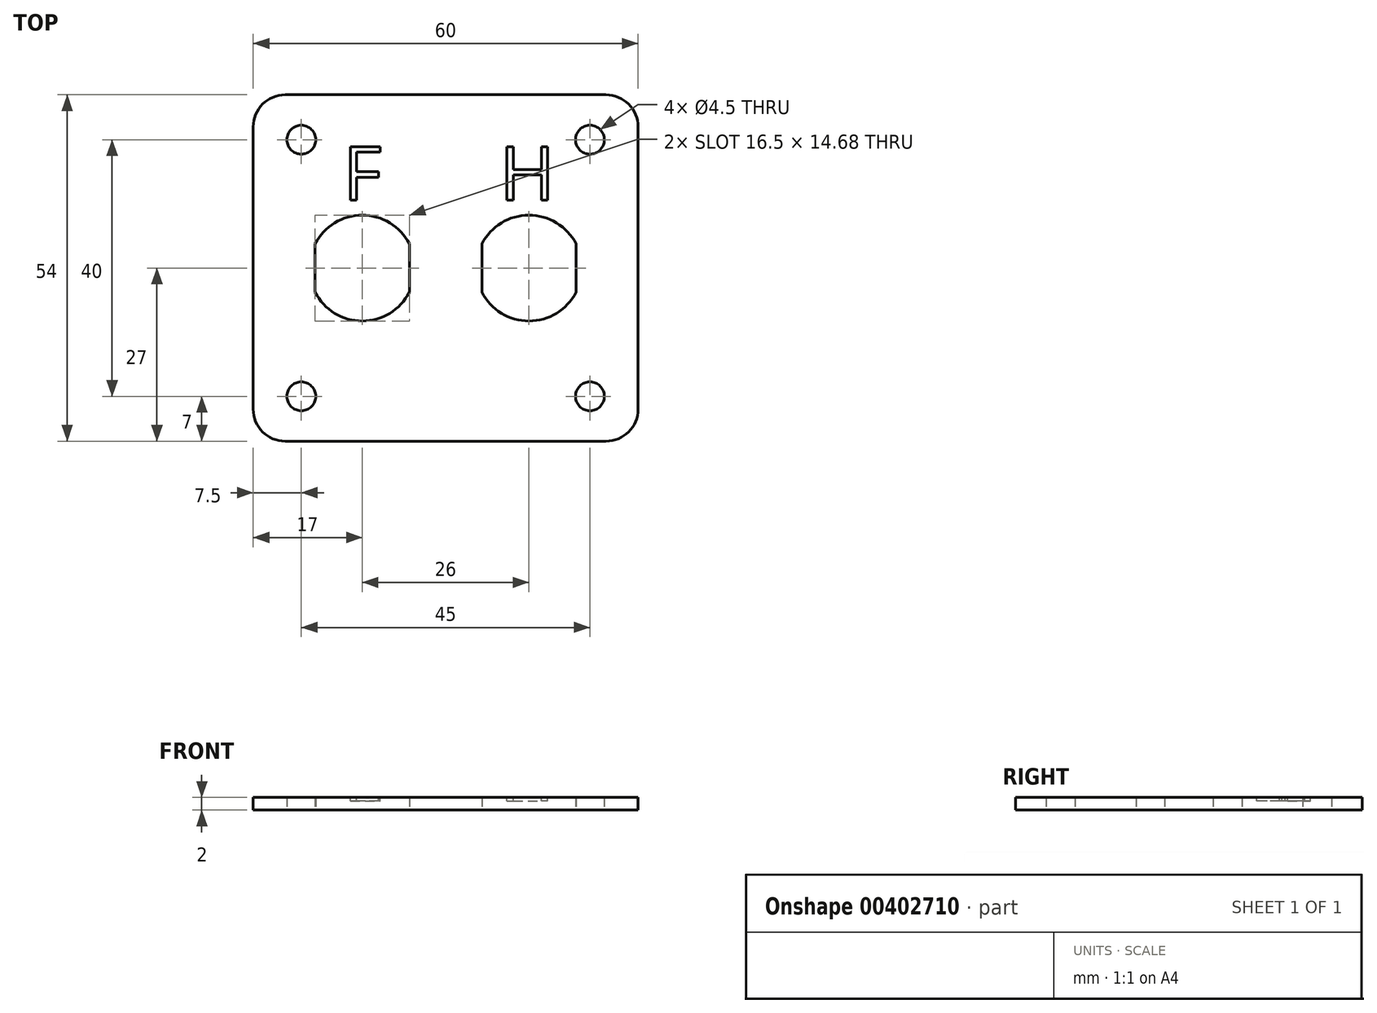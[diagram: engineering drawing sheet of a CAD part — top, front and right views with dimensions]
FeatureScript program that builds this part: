
annotation { "Feature Type Name" : "Feature", "Feature Type Description" : "" }
export const myFeature = defineFeature(function(context is Context, id is Id, definition is map)
    precondition{}
    {
        {
            var Q0;
            Q0=qCreatedBy(makeId("Top.planeOp"),FACE);
            var sketch = newSketch(context, id + "F0", { "sketchPlane" : qUnion([Q0])});
            skLineSegment(sketch, "E0.bottom", {"start": v(30, -27) * mm, "end": v(-30, -27) * mm});
            skLineSegment(sketch, "E0.top", {"start": v(30, 27) * mm, "end": v(-30, 27) * mm});
            skLineSegment(sketch, "E0.left", {"start": v(30, -27) * mm, "end": v(30, 27) * mm});
            skLineSegment(sketch, "E0.right", {"start": v(-30, -27) * mm, "end": v(-30, 27) * mm});
            skPoint(sketch, "E0.middle", {"position": v(0, 0) * mm});
            skLineSegment(sketch, "E1.bottom", {"start": v(22.5, -20) * mm, "end": v(-22.5, -20) * mm});
            skLineSegment(sketch, "E1.top", {"start": v(22.5, 20) * mm, "end": v(-22.5, 20) * mm});
            skLineSegment(sketch, "E1.left", {"start": v(22.5, -20) * mm, "end": v(22.5, 20) * mm});
            skLineSegment(sketch, "E1.right", {"start": v(-22.5, -20) * mm, "end": v(-22.5, 20) * mm});
            skPoint(sketch, "E2", {"position": v(13, 0) * mm});
            skPoint(sketch, "E3", {"position": v(-13, 0) * mm});
            skPoint(sketch, "E4", {"position": v(2.46, -38.07) * mm});
            skCircle(sketch, "E5", {"center": v(13, 0) * mm, "radius": 8.25 * mm});
            skCircle(sketch, "E6", {"center": v(-13, 0) * mm, "radius": 8.25 * mm});
            skPoint(sketch, "E7", {"position": v(-22.5, 20) * mm});
            skPoint(sketch, "E8", {"position": v(-22.5, -20) * mm});
            skPoint(sketch, "E9", {"position": v(22.5, -20) * mm});
            skPoint(sketch, "E10", {"position": v(22.5, 20) * mm});
            skLineSegment(sketch, "E11.bottom", {"start": v(-5.66, -3.77) * mm, "end": v(-20.34, -3.77) * mm});
            skLineSegment(sketch, "E11.top", {"start": v(-5.66, 3.77) * mm, "end": v(-20.34, 3.77) * mm});
            skLineSegment(sketch, "E11.left", {"start": v(-5.66, -3.77) * mm, "end": v(-5.66, 3.77) * mm});
            skLineSegment(sketch, "E11.right", {"start": v(-20.34, -3.77) * mm, "end": v(-20.34, 3.77) * mm});
            skLineSegment(sketch, "E12.bottom", {"start": v(5.66, -3.77) * mm, "end": v(20.34, -3.77) * mm});
            skLineSegment(sketch, "E12.top", {"start": v(5.66, 3.77) * mm, "end": v(20.34, 3.77) * mm});
            skLineSegment(sketch, "E12.left", {"start": v(5.66, -3.77) * mm, "end": v(5.66, 3.77) * mm});
            skLineSegment(sketch, "E12.right", {"start": v(20.34, -3.77) * mm, "end": v(20.34, 3.77) * mm});
            skSolve(sketch);
        }
        {
            var Q0;
            {var subQ0=sQuery(id+"F0.wireOp",EDGE,"8MdXUvT1-A3xL-WGTa-ljN5-XWlnOgiy7zjZ.right");Q0=makeQuery(id+"F0.imprint","IMPRINT",FACE,{"disambiguationData":[TD([[makeQuery(id+"F0.imprint","IMPRINT",EDGE,{"derivedFrom":subQ0}),1.0]])]});}
            var Q1;
            {var subQ0=sQuery(id+"F0.wireOp",EDGE,"wU3xxOYv-X3oH-PTcr-ihHl-F4pvzyvM6u1C.left");Q1=makeQuery(id+"F0.imprint","IMPRINT",FACE,{"disambiguationData":[TD([[makeQuery(id+"F0.imprint","IMPRINT",EDGE,{"derivedFrom":subQ0}),1.0]])]});}
            var Q2;
            {var subQ0=sQuery(id+"F0.wireOp",EDGE,"wU3xxOYv-X3oH-PTcr-ihHl-F4pvzyvM6u1C.right");Q2=makeQuery(id+"F0.imprint","IMPRINT",FACE,{"disambiguationData":[TD([[makeQuery(id+"F0.imprint","IMPRINT",EDGE,{"derivedFrom":subQ0}),-1.0]])]});}
            var Q3;
            {var subQ0=sQuery(id+"F0.wireOp",EDGE,"8MdXUvT1-A3xL-WGTa-ljN5-XWlnOgiy7zjZ.left");Q3=makeQuery(id+"F0.imprint","IMPRINT",FACE,{"disambiguationData":[TD([[makeQuery(id+"F0.imprint","IMPRINT",EDGE,{"derivedFrom":subQ0}),-1.0]])]});}
            var Q4;
            Q4=makeQuery(id+"F0.imprint","IMPRINT",FACE,{"disambiguationData":[TD([[makeQuery(id+"F0.imprint","IMPRINT",EDGE,{"derivedFrom":sQuery(id+"F0.wireOp",EDGE,"E1.bottom")}),-1.0]])]});
            var Q5;
            Q5=makeQuery(id+"F0.imprint","IMPRINT",FACE,{"disambiguationData":[TD([[makeQuery(id+"F0.imprint","IMPRINT",EDGE,{"derivedFrom":sQuery(id+"F0.wireOp",EDGE,"E0.bottom")}),-1.0]])]});
            var Q6;
            {var subQ0=sQuery(id+"F0.wireOp",EDGE,"E11.right");Q6=makeQuery(id+"F0.imprint","IMPRINT",FACE,{"disambiguationData":[TD([[makeQuery(id+"F0.imprint","IMPRINT",EDGE,{"derivedFrom":subQ0}),1.0]])]});}
            var Q7;
            {var subQ0=sQuery(id+"F0.wireOp",EDGE,"E11.left");Q7=makeQuery(id+"F0.imprint","IMPRINT",FACE,{"disambiguationData":[TD([[makeQuery(id+"F0.imprint","IMPRINT",EDGE,{"derivedFrom":subQ0}),-1.0]])]});}
            var Q8;
            {var subQ0=sQuery(id+"F0.wireOp",EDGE,"E12.left");Q8=makeQuery(id+"F0.imprint","IMPRINT",FACE,{"disambiguationData":[TD([[makeQuery(id+"F0.imprint","IMPRINT",EDGE,{"derivedFrom":subQ0}),1.0]])]});}
            var Q9;
            {var subQ0=sQuery(id+"F0.wireOp",EDGE,"E12.right");Q9=makeQuery(id+"F0.imprint","IMPRINT",FACE,{"disambiguationData":[TD([[makeQuery(id+"F0.imprint","IMPRINT",EDGE,{"derivedFrom":subQ0}),-1.0]])]});}
            extrude(context, id + "F1", {"entities" : qUnion([Q0, Q1, Q2, Q3, Q4, Q5, Q6, Q7, Q8, Q9]), "depth" : 2 * mm});
        }
        {
            var Q0;
            Q0=sQuery(id+"F0.wireOp",VERTEX,"E7");
            var Q1;
            Q1=sQuery(id+"F0.wireOp",VERTEX,"E8");
            var Q2;
            Q2=sQuery(id+"F0.wireOp",VERTEX,"E9");
            var Q3;
            Q3=sQuery(id+"F0.wireOp",VERTEX,"E10");
            var Q4;
            Q4=makeQuery(id+"F1.opExtrude","SWEPT_BODY",BODY,{"disambiguationData":[OSD([sQuery(id+"F0.wireOp",EDGE,"E0.bottom"),sQuery(id+"F0.wireOp",EDGE,"E0.top"),sQuery(id+"F0.wireOp",EDGE,"E0.left"),sQuery(id+"F0.wireOp",EDGE,"E0.right"),sQuery(id+"F0.wireOp",EDGE,"E5"),sQuery(id+"F0.wireOp",EDGE,"E6"),sQuery(id+"F0.wireOp",EDGE,"8MdXUvT1-A3xL-WGTa-ljN5-XWlnOgiy7zjZ.left"),sQuery(id+"F0.wireOp",EDGE,"8MdXUvT1-A3xL-WGTa-ljN5-XWlnOgiy7zjZ.right"),sQuery(id+"F0.wireOp",EDGE,"wU3xxOYv-X3oH-PTcr-ihHl-F4pvzyvM6u1C.left"),sQuery(id+"F0.wireOp",EDGE,"wU3xxOYv-X3oH-PTcr-ihHl-F4pvzyvM6u1C.right")])]});
            hole(context, id + "F2", {"style" : HoleStyle.SIMPLE, "endStyle" : HoleEndStyle.THROUGH, "oppositeDirection" : true, "holeDiameter" : 4.5 * mm, "isTappedThrough" : true, "tappedDepth" : 12 * mm, "tapClearance" : 3, "locations" : qUnion([Q0, Q1, Q2, Q3]), "scope" : qUnion([Q4])});
        }
        {
            var Q0;
            Q0=makeQuery(id+"F1.opExtrude","SWEPT_EDGE",EDGE,{"disambiguationData":[OSD([sQuery(id+"F0.wireOp",EDGE,"E0.bottom"),sQuery(id+"F0.wireOp",EDGE,"E0.right")])]});
            var Q1;
            Q1=makeQuery(id+"F1.opExtrude","SWEPT_EDGE",EDGE,{"disambiguationData":[OSD([sQuery(id+"F0.wireOp",EDGE,"E0.bottom"),sQuery(id+"F0.wireOp",EDGE,"E0.left")])]});
            var Q2;
            Q2=makeQuery(id+"F1.opExtrude","SWEPT_EDGE",EDGE,{"disambiguationData":[OSD([sQuery(id+"F0.wireOp",EDGE,"E0.top"),sQuery(id+"F0.wireOp",EDGE,"E0.left")])]});
            var Q3;
            Q3=makeQuery(id+"F1.opExtrude","SWEPT_EDGE",EDGE,{"disambiguationData":[OSD([sQuery(id+"F0.wireOp",EDGE,"E0.top"),sQuery(id+"F0.wireOp",EDGE,"E0.right")])]});
            fillet(context, id + "F3", {"entities" : qUnion([Q0, Q1, Q2, Q3]), "radius" : 5 * mm, "tangentPropagation" : true, "allowEdgeOverflow" : false});
        }
        {
            var Q0;
            Q0=makeQuery(id+"F1.opExtrude","CAP_FACE",FACE,{"disambiguationData":[OSD([sQuery(id+"F0.wireOp",EDGE,"E0.bottom"),sQuery(id+"F0.wireOp",EDGE,"E0.top"),sQuery(id+"F0.wireOp",EDGE,"E0.left"),sQuery(id+"F0.wireOp",EDGE,"E0.right"),sQuery(id+"F0.wireOp",EDGE,"E5"),sQuery(id+"F0.wireOp",EDGE,"E6"),sQuery(id+"F0.wireOp",EDGE,"E11.left"),sQuery(id+"F0.wireOp",EDGE,"E11.right"),sQuery(id+"F0.wireOp",EDGE,"E12.left"),sQuery(id+"F0.wireOp",EDGE,"E12.right")])],"isStart":false});
            var sketch = newSketch(context, id + "F4", { "sketchPlane" : qUnion([Q0])});
            skText(sketch, "E13", { "text": "F", "fontName": "OpenSans-Regular.ttf"});
            skText(sketch, "E14", { "text": "H", "fontName": "OpenSans-Regular.ttf"});
            const initialGuessF4  = {"E13": [-0.01602, 0.01057, 1, 0, 0.00843], "E14": [0.00841, 0.01057, 1, 0, 0.00843]};
            skSetInitialGuess(sketch, initialGuessF4);
            skSolve(sketch);
        }
        {
            var Q0;
            Q0=makeQuery(id+"F4.imprint","IMPRINT",FACE,{"disambiguationData":[TD([[makeQuery(id+"F4.imprint","IMPRINT",EDGE,{"derivedFrom":sQuery(id+"F4.wireOp",EDGE,"E13.sketch_text.stroke-0")}),-1.0]])]});
            var Q1;
            Q1=makeQuery(id+"F4.imprint","IMPRINT",FACE,{"disambiguationData":[TD([[makeQuery(id+"F4.imprint","IMPRINT",EDGE,{"derivedFrom":sQuery(id+"F4.wireOp",EDGE,"E14.sketch_text.stroke-0")}),-1.0]])]});
            extrude(context, id + "F5", {"entities" : qUnion([Q0, Q1]), "operationType" : NewBodyOperationType.REMOVE, "oppositeDirection" : true, "depth" : 0.6 * mm});
        }
    });
